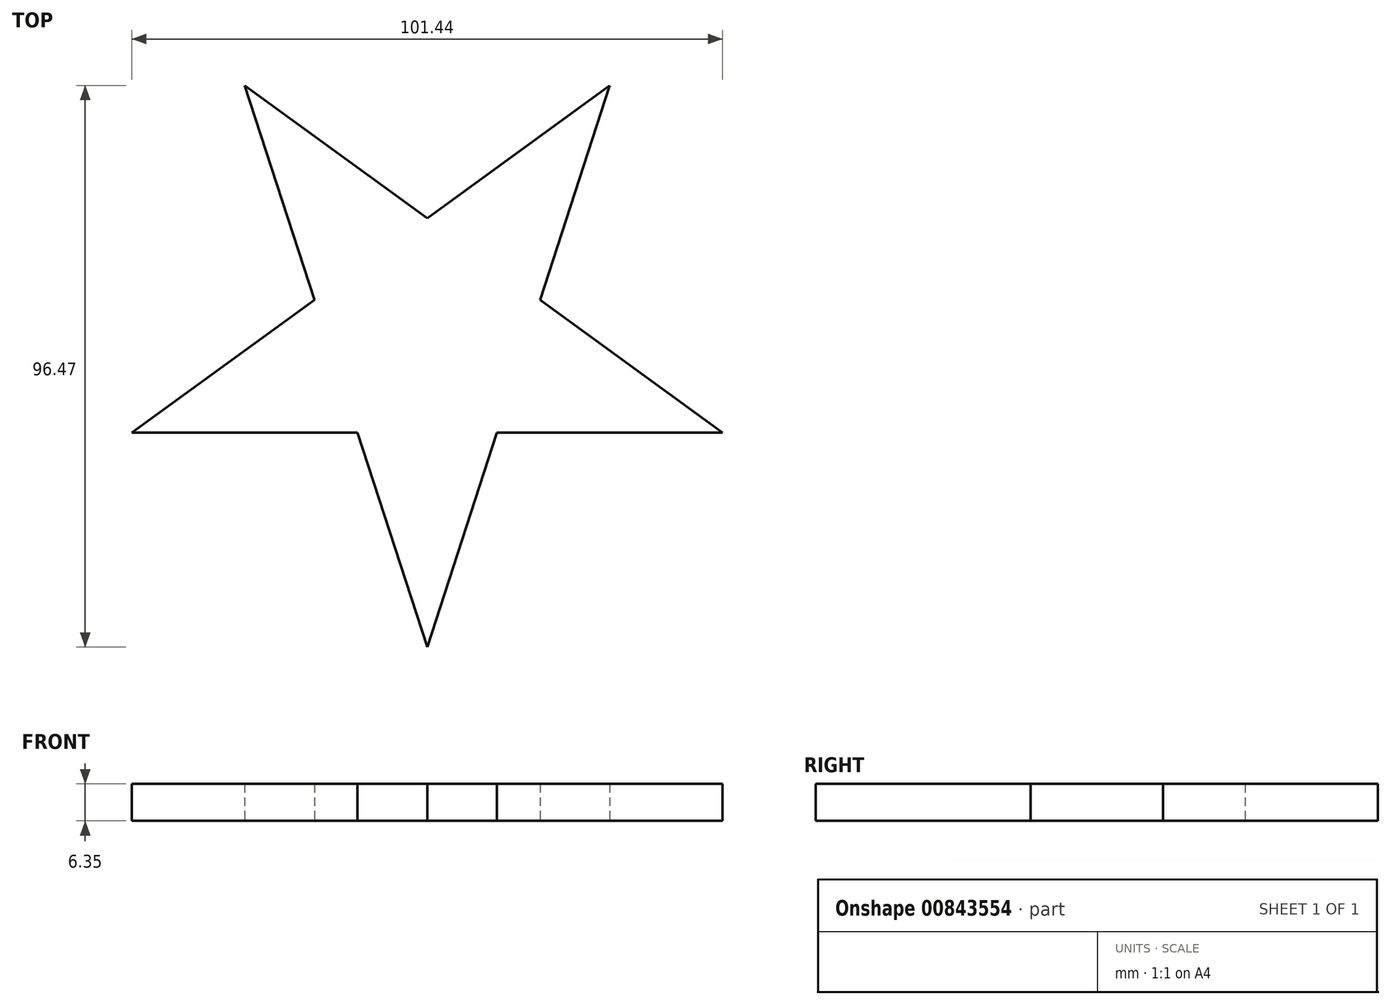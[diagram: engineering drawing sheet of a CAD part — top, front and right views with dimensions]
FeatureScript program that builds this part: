
annotation { "Feature Type Name" : "Feature", "Feature Type Description" : "" }
export const myFeature = defineFeature(function(context is Context, id is Id, definition is map)
    precondition{}
    {
        {
            var Q0;
            Q0=qCreatedBy(makeId("Top.planeOp"),FACE);
            var sketch = newSketch(context, id + "F0", { "sketchPlane" : qUnion([Q0])});
            skLineSegment(sketch, "E0.bottom", {"start": v(50.8, -50.8) * mm, "end": v(-50.8, -50.8) * mm, "construction": true});
            skLineSegment(sketch, "E0.top", {"start": v(50.8, 50.8) * mm, "end": v(-50.8, 50.8) * mm, "construction": true});
            skLineSegment(sketch, "E0.left", {"start": v(50.8, -50.8) * mm, "end": v(50.8, 50.8) * mm, "construction": true});
            skLineSegment(sketch, "E0.right", {"start": v(-50.8, -50.8) * mm, "end": v(-50.8, 50.8) * mm, "construction": true});
            skPoint(sketch, "E0.middle", {"position": v(0, 0) * mm});
            skCircle(sketch, "E1.cCircle", {"center": v(0, 0) * mm, "radius": 43.14 * mm, "construction": true});
            skLineSegment(sketch, "E1.0", {"start": v(-31.35, 43.14) * mm, "end": v(31.35, 43.14) * mm, "construction": true});
            skLineSegment(sketch, "E1.1", {"start": v(31.35, 43.14) * mm, "end": v(50.72, -16.48) * mm, "construction": true});
            skLineSegment(sketch, "E1.2", {"start": v(50.72, -16.48) * mm, "end": v(0, -53.33) * mm, "construction": true});
            skLineSegment(sketch, "E1.3", {"start": v(0, -53.33) * mm, "end": v(-50.72, -16.48) * mm, "construction": true});
            skLineSegment(sketch, "E1.4", {"start": v(-50.72, -16.48) * mm, "end": v(-31.35, 43.14) * mm, "construction": true});
            skPoint(sketch, "E1.0.midPoint", {"position": v(0, 43.14) * mm});
            skLineSegment(sketch, "E2", {"start": v(-31.35, 43.14) * mm, "end": v(0, -53.33) * mm, "construction": true});
            skLineSegment(sketch, "E3", {"start": v(31.35, 43.14) * mm, "end": v(0, -53.33) * mm, "construction": true});
            skLineSegment(sketch, "E4", {"start": v(-50.72, -16.48) * mm, "end": v(50.72, -16.48) * mm, "construction": true});
            skLineSegment(sketch, "E5", {"start": v(-31.35, 43.14) * mm, "end": v(50.72, -16.48) * mm, "construction": true});
            skLineSegment(sketch, "E6", {"start": v(-50.72, -16.48) * mm, "end": v(31.35, 43.14) * mm, "construction": true});
            skLineSegment(sketch, "E7", {"start": v(-31.35, 43.14) * mm, "end": v(-19.37, 6.3) * mm});
            skLineSegment(sketch, "E8", {"start": v(-19.37, 6.3) * mm, "end": v(-50.72, -16.48) * mm});
            skLineSegment(sketch, "E9", {"start": v(-11.97, -16.48) * mm, "end": v(0, -53.33) * mm});
            skLineSegment(sketch, "E10", {"start": v(11.97, -16.48) * mm, "end": v(50.72, -16.48) * mm});
            skLineSegment(sketch, "E11", {"start": v(19.37, 6.3) * mm, "end": v(31.35, 43.14) * mm});
            skLineSegment(sketch, "E12", {"start": v(0, 20.37) * mm, "end": v(-31.35, 43.14) * mm});
            skLineSegment(sketch, "E13", {"start": v(0, 20.37) * mm, "end": v(31.35, 43.14) * mm});
            skLineSegment(sketch, "E14", {"start": v(0, -53.33) * mm, "end": v(11.97, -16.48) * mm});
            skLineSegment(sketch, "E15", {"start": v(50.72, -16.48) * mm, "end": v(19.37, 6.3) * mm});
            skLineSegment(sketch, "E16", {"start": v(-50.72, -16.48) * mm, "end": v(-10.12, -16.48) * mm});
            skSolve(sketch);
        }
        {
            var Q0;
            Q0=qSketchRegion(id+"F0",true);
            extrude(context, id + "F1", {"entities" : qUnion([Q0]), "depth" : 6.35 * mm, "offsetDistance" : 25.4 * mm});
        }
    });
